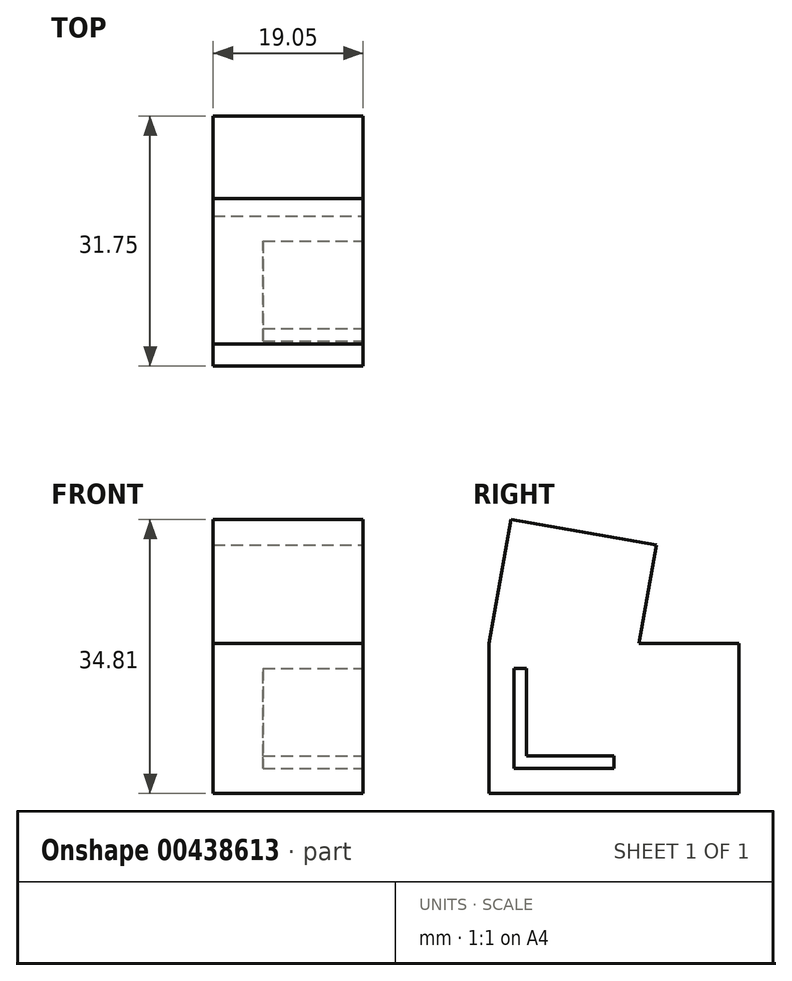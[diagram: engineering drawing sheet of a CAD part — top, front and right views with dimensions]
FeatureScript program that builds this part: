
annotation { "Feature Type Name" : "Feature", "Feature Type Description" : "" }
export const myFeature = defineFeature(function(context is Context, id is Id, definition is map)
    precondition{}
    {
        {
            var Q0;
            Q0=qCreatedBy(makeId("Top.planeOp"),FACE);
            var sketch = newSketch(context, id + "F0", { "sketchPlane" : qUnion([Q0])});
            skLineSegment(sketch, "E0", {"start": v(0, 0) * mm, "end": v(0, 19.05) * mm});
            skLineSegment(sketch, "E1", {"start": v(0, 19.05) * mm, "end": v(19.05, 19.05) * mm});
            skLineSegment(sketch, "E2", {"start": v(19.05, 19.05) * mm, "end": v(19.05, 0) * mm});
            skLineSegment(sketch, "E3", {"start": v(19.05, 0) * mm, "end": v(0, 0) * mm});
            skSolve(sketch);
        }
        {
            var Q0;
            Q0 = qSketchRegion(id + "F0", true);
            extrude(context, id + "F1", {"entities" : qUnion([Q0]), "depth" : 19.05 * mm});
        }
        {
            var Q0;
            Q0=makeQuery(id+"F1.opExtrude","SWEPT_FACE",FACE,{"disambiguationData":[OSD([sQuery(id+"F0.wireOp",EDGE,"E2")])]});
            var sketch = newSketch(context, id + "F2", { "sketchPlane" : qUnion([Q0])});
            skLineSegment(sketch, "E4", {"start": v(3.17, 15.88) * mm, "end": v(3.18, 3.17) * mm});
            skLineSegment(sketch, "E5", {"start": v(3.18, 3.17) * mm, "end": v(15.88, 3.18) * mm});
            skLineSegment(sketch, "E6", {"start": v(15.88, 3.18) * mm, "end": v(15.88, 4.76) * mm});
            skLineSegment(sketch, "E7", {"start": v(15.88, 4.76) * mm, "end": v(4.76, 4.76) * mm});
            skLineSegment(sketch, "E8", {"start": v(4.76, 4.76) * mm, "end": v(4.76, 15.88) * mm});
            skLineSegment(sketch, "E9", {"start": v(4.76, 15.88) * mm, "end": v(3.17, 15.88) * mm});
            skSolve(sketch);
        }
        {
            var Q0;
            Q0=makeQuery(id+"F2.imprint","IMPRINT",FACE,{"disambiguationData":[TD([[makeQuery(id+"F2.imprint","IMPRINT",EDGE,{"derivedFrom":sQuery(id+"F2.wireOp",EDGE,"E4")}),1.0]])]});
            extrude(context, id + "F3", {"entities" : qUnion([Q0]), "operationType" : NewBodyOperationType.REMOVE, "oppositeDirection" : true, "depth" : 12.7 * mm});
        }
        {
            var Q0;
            Q0=makeQuery(id+"F1.opExtrude","SWEPT_FACE",FACE,{"disambiguationData":[OSD([sQuery(id+"F0.wireOp",EDGE,"E2")])]});
            var sketch = newSketch(context, id + "F4", { "sketchPlane" : qUnion([Q0])});
            skLineSegment(sketch, "E10", {"start": v(0, 19.05) * mm, "end": v(2.78, 34.81) * mm});
            skLineSegment(sketch, "E11", {"start": v(2.78, 34.81) * mm, "end": v(21.26, 31.56) * mm});
            skLineSegment(sketch, "E12", {"start": v(21.26, 31.56) * mm, "end": v(19.05, 19.05) * mm});
            skSolve(sketch);
        }
        {
            var Q0;
            Q0=makeQuery(id+"F4.imprint","IMPRINT",FACE,{"disambiguationData":[TD([[makeQuery(id+"F4.imprint","IMPRINT",EDGE,{"derivedFrom":sQuery(id+"F4.wireOp",EDGE,"E10")}),-1.0]])]});
            extrude(context, id + "F5", {"entities" : qUnion([Q0]), "operationType" : NewBodyOperationType.ADD, "oppositeDirection" : true, "depth" : 19.05 * mm});
        }
        {
            var Q0;
            Q0=makeQuery(id+"F1.opExtrude","SWEPT_FACE",FACE,{"disambiguationData":[OSD([sQuery(id+"F0.wireOp",EDGE,"E1")])]});
            extrude(context, id + "F6", {"entities" : qUnion([Q0]), "operationType" : NewBodyOperationType.ADD, "depth" : 12.7 * mm});
        }
    });
